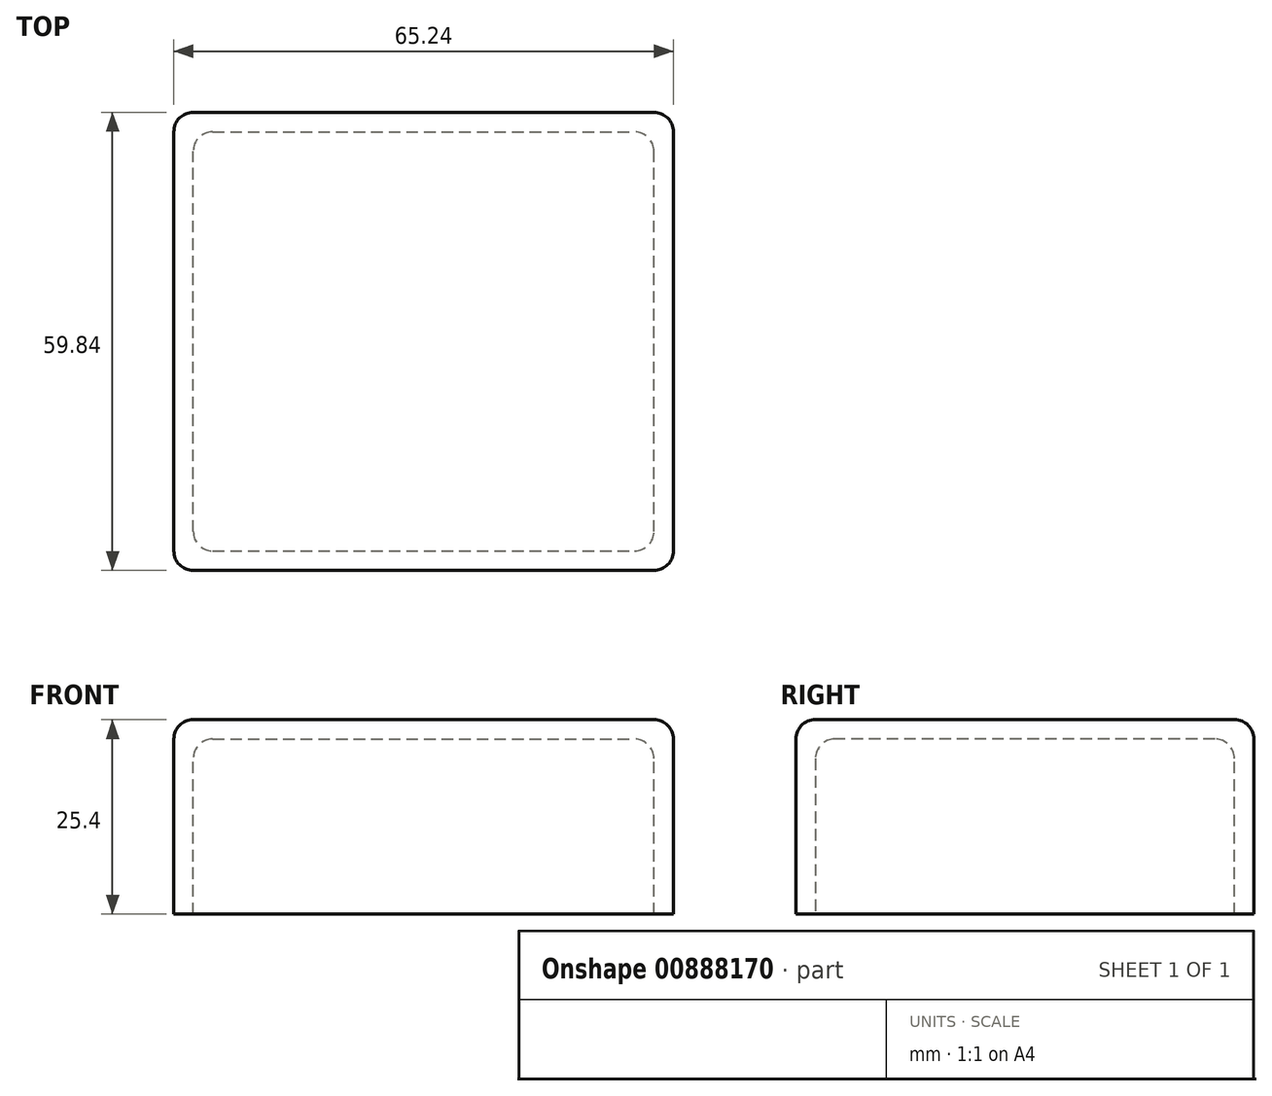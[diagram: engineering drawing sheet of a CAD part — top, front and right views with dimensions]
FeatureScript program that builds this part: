
annotation { "Feature Type Name" : "Feature", "Feature Type Description" : "" }
export const myFeature = defineFeature(function(context is Context, id is Id, definition is map)
    precondition{}
    {
        {
            var Q0;
            Q0=qCreatedBy(makeId("Top.planeOp"),FACE);
            var sketch = newSketch(context, id + "F0", { "sketchPlane" : qUnion([Q0])});
            skLineSegment(sketch, "E0.bottom", {"start": v(0, 0) * mm, "end": v(65.24, 0) * mm});
            skLineSegment(sketch, "E0.top", {"start": v(0, 59.84) * mm, "end": v(65.24, 59.84) * mm});
            skLineSegment(sketch, "E0.left", {"start": v(0, 0) * mm, "end": v(0, 59.84) * mm});
            skLineSegment(sketch, "E0.right", {"start": v(65.24, 0) * mm, "end": v(65.24, 59.84) * mm});
            skSolve(sketch);
        }
        {
            var Q0;
            Q0 = qSketchRegion(id + "F0", true);
            extrude(context, id + "F1", {"entities" : qUnion([Q0]), "depth" : 25.4 * mm, "offsetDistance" : 25.4 * mm});
        }
        {
            var Q0;
            Q0=makeQuery(id+"F1.opExtrude","CAP_EDGE",EDGE,{"disambiguationData":[OSD([sQuery(id+"F0.wireOp",EDGE,"E0.bottom")])],"isStart":false});
            var Q1;
            Q1=makeQuery(id+"F1.opExtrude","CAP_EDGE",EDGE,{"disambiguationData":[OSD([sQuery(id+"F0.wireOp",EDGE,"E0.right")])],"isStart":false});
            var Q2;
            Q2=makeQuery(id+"F1.opExtrude","CAP_EDGE",EDGE,{"disambiguationData":[OSD([sQuery(id+"F0.wireOp",EDGE,"E0.top")])],"isStart":false});
            var Q3;
            Q3=makeQuery(id+"F1.opExtrude","CAP_EDGE",EDGE,{"disambiguationData":[OSD([sQuery(id+"F0.wireOp",EDGE,"E0.left")])],"isStart":false});
            var Q4;
            Q4=makeQuery(id+"F1.opExtrude","SWEPT_EDGE",EDGE,{"disambiguationData":[OSD([sQuery(id+"F0.wireOp",EDGE,"E0.bottom"),sQuery(id+"F0.wireOp",EDGE,"E0.right")])]});
            var Q5;
            Q5=makeQuery(id+"F1.opExtrude","SWEPT_EDGE",EDGE,{"disambiguationData":[OSD([sQuery(id+"F0.wireOp",EDGE,"E0.bottom"),sQuery(id+"F0.wireOp",EDGE,"E0.left")])]});
            var Q6;
            Q6=makeQuery(id+"F1.opExtrude","SWEPT_EDGE",EDGE,{"disambiguationData":[OSD([sQuery(id+"F0.wireOp",EDGE,"E0.top"),sQuery(id+"F0.wireOp",EDGE,"E0.right")])]});
            var Q7;
            Q7=makeQuery(id+"F1.opExtrude","SWEPT_EDGE",EDGE,{"disambiguationData":[OSD([sQuery(id+"F0.wireOp",EDGE,"E0.top"),sQuery(id+"F0.wireOp",EDGE,"E0.left")])]});
            fillet(context, id + "F2", {"entities" : qUnion([Q0, Q1, Q2, Q3, Q4, Q5, Q6, Q7]), "radius" : 2.54 * mm, "tangentPropagation" : true, "allowEdgeOverflow" : false});
        }
        {
            var Q0;
            Q0=makeQuery(id+"F1.opExtrude","CAP_FACE",FACE,{"disambiguationData":[OSD([sQuery(id+"F0.wireOp",EDGE,"E0.bottom"),sQuery(id+"F0.wireOp",EDGE,"E0.top"),sQuery(id+"F0.wireOp",EDGE,"E0.left"),sQuery(id+"F0.wireOp",EDGE,"E0.right")])],"isStart":true});
            shell(context, id + "F3", {"entities" : qUnion([Q0]), "thickness" : 2.54 * mm});
        }
        {
            var Q0;
            Q0=makeQuery(id+"F3.opShell","OFFSET_EDGE",EDGE,{"disambiguationData":[OSD([sQuery(id+"F0.wireOp",EDGE,"E0.top"),sQuery(id+"F0.wireOp",EDGE,"E0.right")])]});
            var Q1;
            Q1=makeQuery(id+"F3.opShell","OFFSET_EDGE",EDGE,{"disambiguationData":[OSD([sQuery(id+"F0.wireOp",EDGE,"E0.bottom"),sQuery(id+"F0.wireOp",EDGE,"E0.right")])]});
            var Q2;
            Q2=makeQuery(id+"F3.opShell","OFFSET_EDGE",EDGE,{"disambiguationData":[OSD([sQuery(id+"F0.wireOp",EDGE,"E0.bottom"),sQuery(id+"F0.wireOp",EDGE,"E0.left")])]});
            var Q3;
            Q3=makeQuery(id+"F3.opShell","OFFSET_EDGE",EDGE,{"disambiguationData":[OSD([sQuery(id+"F0.wireOp",EDGE,"E0.top"),sQuery(id+"F0.wireOp",EDGE,"E0.left")])]});
            var Q4;
            Q4=makeQuery(id+"F3.opShell","OFFSET_FACE",FACE,{"disambiguationData":[OSD([sQuery(id+"F0.wireOp",EDGE,"E0.bottom"),sQuery(id+"F0.wireOp",EDGE,"E0.top"),sQuery(id+"F0.wireOp",EDGE,"E0.left"),sQuery(id+"F0.wireOp",EDGE,"E0.right")])]});
            fillet(context, id + "F4", {"entities" : qUnion([Q0, Q1, Q2, Q3, Q4]), "radius" : 2.54 * mm, "tangentPropagation" : true, "allowEdgeOverflow" : false});
        }
    });
